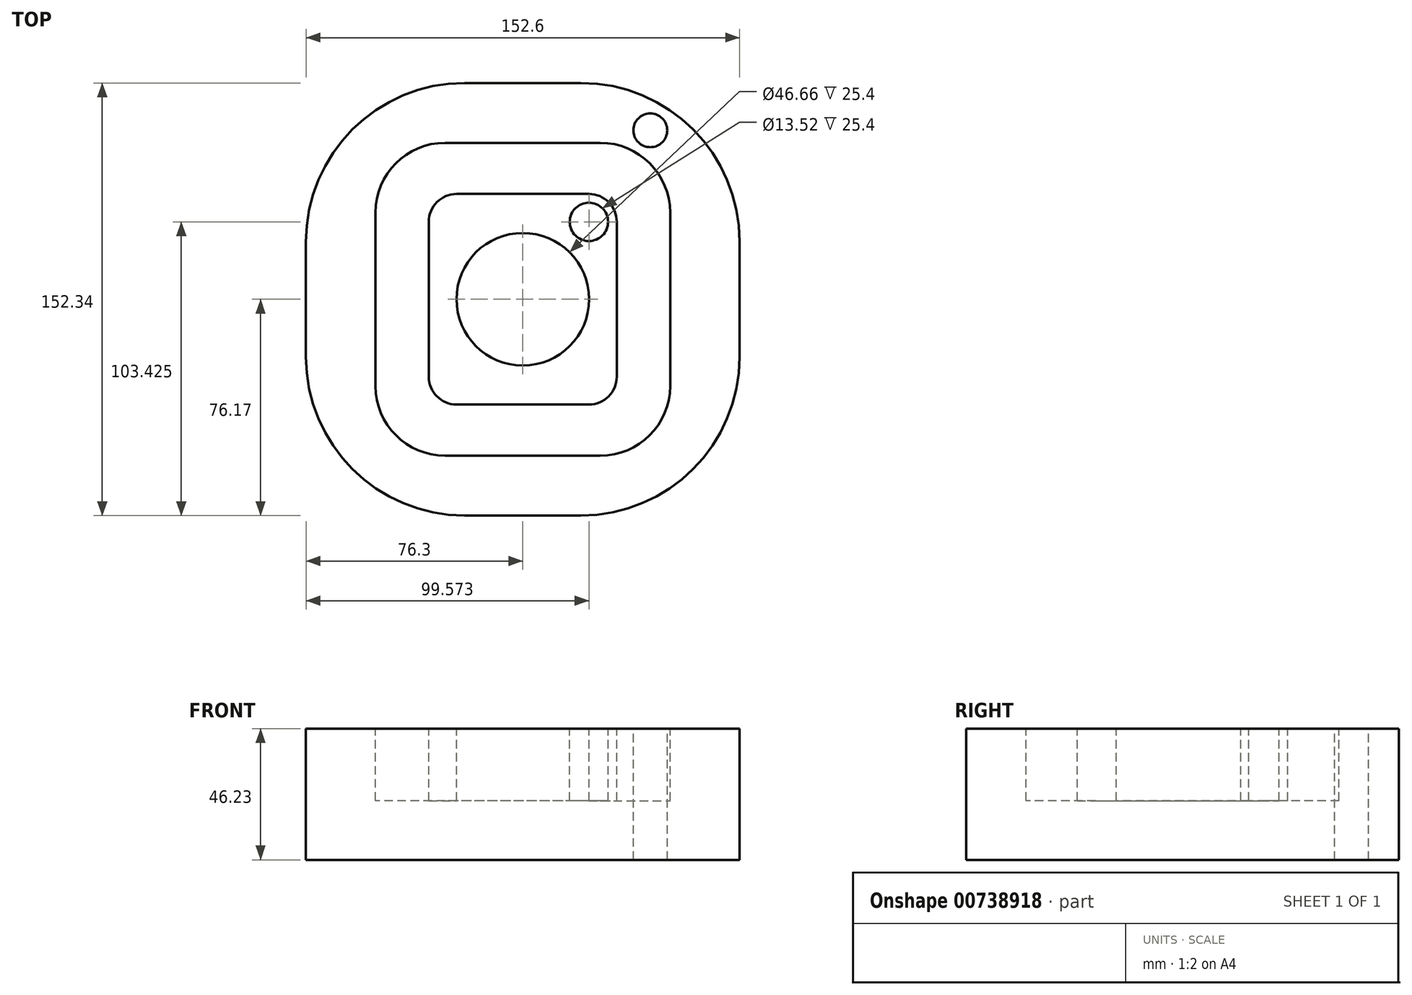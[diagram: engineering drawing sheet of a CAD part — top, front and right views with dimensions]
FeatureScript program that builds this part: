
annotation { "Feature Type Name" : "Feature", "Feature Type Description" : "" }
export const myFeature = defineFeature(function(context is Context, id is Id, definition is map)
    precondition{}
    {
        {
            var Q0;
            Q0=qCreatedBy(makeId("Top.planeOp"),FACE);
            var sketch = newSketch(context, id + "F0", { "sketchPlane" : qUnion([Q0])});
            skLineSegment(sketch, "E0.bottom", {"start": v(76.3, -76.17) * mm, "end": v(-76.3, -76.17) * mm});
            skLineSegment(sketch, "E0.top", {"start": v(76.3, 76.17) * mm, "end": v(-76.3, 76.17) * mm});
            skLineSegment(sketch, "E0.left", {"start": v(76.3, -76.17) * mm, "end": v(76.3, 76.17) * mm});
            skLineSegment(sketch, "E0.right", {"start": v(-76.3, -76.17) * mm, "end": v(-76.3, 76.17) * mm});
            skPoint(sketch, "E0.middle", {"position": v(0, 0) * mm});
            skSolve(sketch);
        }
        {
            var Q0;
            Q0=makeQuery(id+"F0.imprint","IMPRINT",FACE,{"disambiguationData":[TD([[makeQuery(id+"F0.imprint","IMPRINT",EDGE,{"derivedFrom":sQuery(id+"F0.wireOp",EDGE,"E0.bottom")}),-1.0]])]});
            extrude(context, id + "F1", {"entities" : qUnion([Q0]), "depth" : 46.23 * mm, "offsetDistance" : 25.4 * mm});
        }
        {
            var Q0;
            Q0=makeQuery(id+"F1.opExtrude","SWEPT_EDGE",EDGE,{"disambiguationData":[OSD([sQuery(id+"F0.wireOp",EDGE,"E0.top"),sQuery(id+"F0.wireOp",EDGE,"E0.left")])]});
            fillet(context, id + "F2", {"entities" : qUnion([Q0]), "radius" : 55.88 * mm, "tangentPropagation" : true, "allowEdgeOverflow" : false});
        }
        {
            var Q0;
            Q0=makeQuery(id+"F1.opExtrude","SWEPT_EDGE",EDGE,{"disambiguationData":[OSD([sQuery(id+"F0.wireOp",EDGE,"E0.top"),sQuery(id+"F0.wireOp",EDGE,"E0.right")])]});
            fillet(context, id + "F3", {"entities" : qUnion([Q0]), "radius" : 55.88 * mm, "tangentPropagation" : true, "allowEdgeOverflow" : false});
        }
        {
            var Q0;
            Q0=makeQuery(id+"F1.opExtrude","SWEPT_EDGE",EDGE,{"disambiguationData":[OSD([sQuery(id+"F0.wireOp",EDGE,"E0.bottom"),sQuery(id+"F0.wireOp",EDGE,"E0.right")])]});
            fillet(context, id + "F4", {"entities" : qUnion([Q0]), "radius" : 55.88 * mm, "tangentPropagation" : true, "allowEdgeOverflow" : false});
        }
        {
            var Q0;
            Q0=makeQuery(id+"F1.opExtrude","SWEPT_EDGE",EDGE,{"disambiguationData":[OSD([sQuery(id+"F0.wireOp",EDGE,"E0.bottom"),sQuery(id+"F0.wireOp",EDGE,"E0.left")])]});
            fillet(context, id + "F5", {"entities" : qUnion([Q0]), "radius" : 55.88 * mm, "tangentPropagation" : true, "allowEdgeOverflow" : false});
        }
        {
            var Q0;
            Q0=makeQuery(id+"F1.opExtrude","CAP_FACE",FACE,{"disambiguationData":[OSD([sQuery(id+"F0.wireOp",EDGE,"E0.bottom"),sQuery(id+"F0.wireOp",EDGE,"E0.top"),sQuery(id+"F0.wireOp",EDGE,"E0.left"),sQuery(id+"F0.wireOp",EDGE,"E0.right")])],"isStart":false});
            var sketch = newSketch(context, id + "F6", { "sketchPlane" : qUnion([Q0])});
            skLineSegment(sketch, "E1.bottom", {"start": v(51.85, -55.08) * mm, "end": v(-51.85, -55.08) * mm});
            skLineSegment(sketch, "E1.top", {"start": v(51.85, 55.08) * mm, "end": v(-51.85, 55.08) * mm});
            skLineSegment(sketch, "E1.left", {"start": v(51.85, -55.08) * mm, "end": v(51.85, 55.08) * mm});
            skLineSegment(sketch, "E1.right", {"start": v(-51.85, -55.08) * mm, "end": v(-51.85, 55.08) * mm});
            skPoint(sketch, "E1.middle", {"position": v(0, 0) * mm});
            skLineSegment(sketch, "E2.bottom", {"start": v(33.08, -37.07) * mm, "end": v(-33.08, -37.07) * mm});
            skLineSegment(sketch, "E2.top", {"start": v(33.08, 37.07) * mm, "end": v(-33.08, 37.07) * mm});
            skLineSegment(sketch, "E2.left", {"start": v(33.08, -37.07) * mm, "end": v(33.08, 37.07) * mm});
            skLineSegment(sketch, "E2.right", {"start": v(-33.08, -37.07) * mm, "end": v(-33.08, 37.07) * mm});
            skSolve(sketch);
        }
        {
            var Q0;
            Q0=makeQuery(id+"F6.imprint","IMPRINT",FACE,{"disambiguationData":[TD([[makeQuery(id+"F6.imprint","IMPRINT",EDGE,{"derivedFrom":sQuery(id+"F6.wireOp",EDGE,"E1.bottom")}),-1.0]])]});
            extrude(context, id + "F7", {"entities" : qUnion([Q0]), "operationType" : NewBodyOperationType.REMOVE, "oppositeDirection" : true, "depth" : 25.4 * mm, "offsetDistance" : 25.4 * mm});
        }
        {
            var Q0;
            Q0=makeQuery(id+"F7.boolean.opBoolean","COPY",EDGE,{"derivedFrom":makeQuery(id+"F7.opExtrude","SWEPT_EDGE",EDGE,{"disambiguationData":[OSD([sQuery(id+"F6.wireOp",EDGE,"E1.bottom"),sQuery(id+"F6.wireOp",EDGE,"E1.right")])]})});
            var Q1;
            Q1=makeQuery(id+"F7.boolean.opBoolean","COPY",EDGE,{"derivedFrom":makeQuery(id+"F7.opExtrude","SWEPT_EDGE",EDGE,{"disambiguationData":[OSD([sQuery(id+"F6.wireOp",EDGE,"E1.bottom"),sQuery(id+"F6.wireOp",EDGE,"E1.left")])]})});
            var Q2;
            Q2=makeQuery(id+"F7.boolean.opBoolean","COPY",EDGE,{"derivedFrom":makeQuery(id+"F7.opExtrude","SWEPT_EDGE",EDGE,{"disambiguationData":[OSD([sQuery(id+"F6.wireOp",EDGE,"E1.top"),sQuery(id+"F6.wireOp",EDGE,"E1.left")])]})});
            var Q3;
            Q3=makeQuery(id+"F7.boolean.opBoolean","COPY",EDGE,{"derivedFrom":makeQuery(id+"F7.opExtrude","SWEPT_EDGE",EDGE,{"disambiguationData":[OSD([sQuery(id+"F6.wireOp",EDGE,"E1.top"),sQuery(id+"F6.wireOp",EDGE,"E1.right")])]})});
            fillet(context, id + "F8", {"entities" : qUnion([Q0, Q1, Q2, Q3]), "radius" : 24.53 * mm, "tangentPropagation" : true, "allowEdgeOverflow" : false});
        }
        {
            var Q0;
            Q0=makeQuery(id+"F7.boolean.opBoolean","COPY",EDGE,{"derivedFrom":makeQuery(id+"F7.opExtrude","SWEPT_EDGE",EDGE,{"disambiguationData":[OSD([sQuery(id+"F6.wireOp",EDGE,"E2.bottom"),sQuery(id+"F6.wireOp",EDGE,"E2.right")])]})});
            var Q1;
            Q1=makeQuery(id+"F7.boolean.opBoolean","COPY",EDGE,{"derivedFrom":makeQuery(id+"F7.opExtrude","SWEPT_EDGE",EDGE,{"disambiguationData":[OSD([sQuery(id+"F6.wireOp",EDGE,"E2.top"),sQuery(id+"F6.wireOp",EDGE,"E2.right")])]})});
            var Q2;
            Q2=makeQuery(id+"F7.boolean.opBoolean","COPY",EDGE,{"derivedFrom":makeQuery(id+"F7.opExtrude","SWEPT_EDGE",EDGE,{"disambiguationData":[OSD([sQuery(id+"F6.wireOp",EDGE,"E2.top"),sQuery(id+"F6.wireOp",EDGE,"E2.left")])]})});
            var Q3;
            Q3=makeQuery(id+"F7.boolean.opBoolean","COPY",EDGE,{"derivedFrom":makeQuery(id+"F7.opExtrude","SWEPT_EDGE",EDGE,{"disambiguationData":[OSD([sQuery(id+"F6.wireOp",EDGE,"E2.bottom"),sQuery(id+"F6.wireOp",EDGE,"E2.left")])]})});
            fillet(context, id + "F9", {"entities" : qUnion([Q0, Q1, Q2, Q3]), "radius" : 9.8 * mm, "tangentPropagation" : true, "allowEdgeOverflow" : false});
        }
        {
            var Q0;
            Q0=makeQuery(id+"F7.boolean.opBoolean","SPLIT",FACE,{"disambiguationData":[TD([makeQuery(id+"F7.opExtrude","SWEPT_FACE",FACE,{"disambiguationData":[OSD([sQuery(id+"F6.wireOp",EDGE,"E2.bottom")])]})])],"derivedFrom":makeQuery(id+"F1.opExtrude","CAP_FACE",FACE,{"disambiguationData":[OSD([sQuery(id+"F0.wireOp",EDGE,"E0.bottom"),sQuery(id+"F0.wireOp",EDGE,"E0.top"),sQuery(id+"F0.wireOp",EDGE,"E0.left"),sQuery(id+"F0.wireOp",EDGE,"E0.right")])],"isStart":false})});
            var sketch = newSketch(context, id + "F10", { "sketchPlane" : qUnion([Q0])});
            skCircle(sketch, "E3", {"center": v(0, 0) * mm, "radius": 23.33 * mm});
            skSolve(sketch);
        }
        {
            var Q0;
            Q0=makeQuery(id+"F10.imprint","IMPRINT",FACE,{"disambiguationData":[TD([[makeQuery(id+"F10.imprint","IMPRINT",EDGE,{"derivedFrom":sQuery(id+"F10.wireOp",EDGE,"E3")}),1.0]])]});
            extrude(context, id + "F11", {"entities" : qUnion([Q0]), "operationType" : NewBodyOperationType.REMOVE, "oppositeDirection" : true, "depth" : 25.4 * mm, "offsetDistance" : 25.4 * mm});
        }
        {
            var Q0;
            Q0=makeQuery(id+"F7.boolean.opBoolean","SPLIT",FACE,{"disambiguationData":[TD([makeQuery(id+"F7.opExtrude","SWEPT_FACE",FACE,{"disambiguationData":[OSD([sQuery(id+"F6.wireOp",EDGE,"E2.bottom")])]})])],"derivedFrom":makeQuery(id+"F1.opExtrude","CAP_FACE",FACE,{"disambiguationData":[OSD([sQuery(id+"F0.wireOp",EDGE,"E0.bottom"),sQuery(id+"F0.wireOp",EDGE,"E0.top"),sQuery(id+"F0.wireOp",EDGE,"E0.left"),sQuery(id+"F0.wireOp",EDGE,"E0.right")])],"isStart":false})});
            var sketch = newSketch(context, id + "F12", { "sketchPlane" : qUnion([Q0])});
            skCircle(sketch, "E4", {"center": v(23.27, 27.25) * mm, "radius": 6.76 * mm});
            skSolve(sketch);
        }
        {
            var Q0;
            Q0=makeQuery(id+"F12.imprint","IMPRINT",FACE,{"disambiguationData":[TD([[makeQuery(id+"F12.imprint","IMPRINT",EDGE,{"derivedFrom":sQuery(id+"F12.wireOp",EDGE,"E4")}),1.0]])]});
            extrude(context, id + "F13", {"entities" : qUnion([Q0]), "operationType" : NewBodyOperationType.REMOVE, "oppositeDirection" : true, "depth" : 25.4 * mm, "offsetDistance" : 25.4 * mm});
        }
        {
            var Q0;
            {var subQ0=sQuery(id+"F0.wireOp",EDGE,"E0.right");var subQ1=sQuery(id+"F0.wireOp",EDGE,"E0.bottom");var subQ2=sQuery(id+"F0.wireOp",EDGE,"E0.left");var subQ3=sQuery(id+"F0.wireOp",EDGE,"E0.top");Q0=makeQuery(id+"F7.boolean.opBoolean","SPLIT",FACE,{"disambiguationData":[TD([makeQuery(id+"F1.opExtrude","SWEPT_FACE",FACE,{"disambiguationData":[OSD([subQ1])]})])],"derivedFrom":makeQuery(id+"F1.opExtrude","CAP_FACE",FACE,{"disambiguationData":[OSD([subQ1,subQ3,subQ2,subQ0])],"isStart":false})});}
            var sketch = newSketch(context, id + "F14", { "sketchPlane" : qUnion([Q0])});
            skCircle(sketch, "E5", {"center": v(44.88, 59.49) * mm, "radius": 5.95 * mm});
            skSolve(sketch);
        }
        {
            var Q0;
            Q0=makeQuery(id+"F14.imprint","IMPRINT",FACE,{"disambiguationData":[TD([[makeQuery(id+"F14.imprint","IMPRINT",EDGE,{"derivedFrom":sQuery(id+"F14.wireOp",EDGE,"E5")}),1.0]])]});
            extrude(context, id + "F15", {"entities" : qUnion([Q0]), "operationType" : NewBodyOperationType.REMOVE, "oppositeDirection" : true, "depth" : 62.48 * mm, "offsetDistance" : 25.4 * mm});
        }
    });
